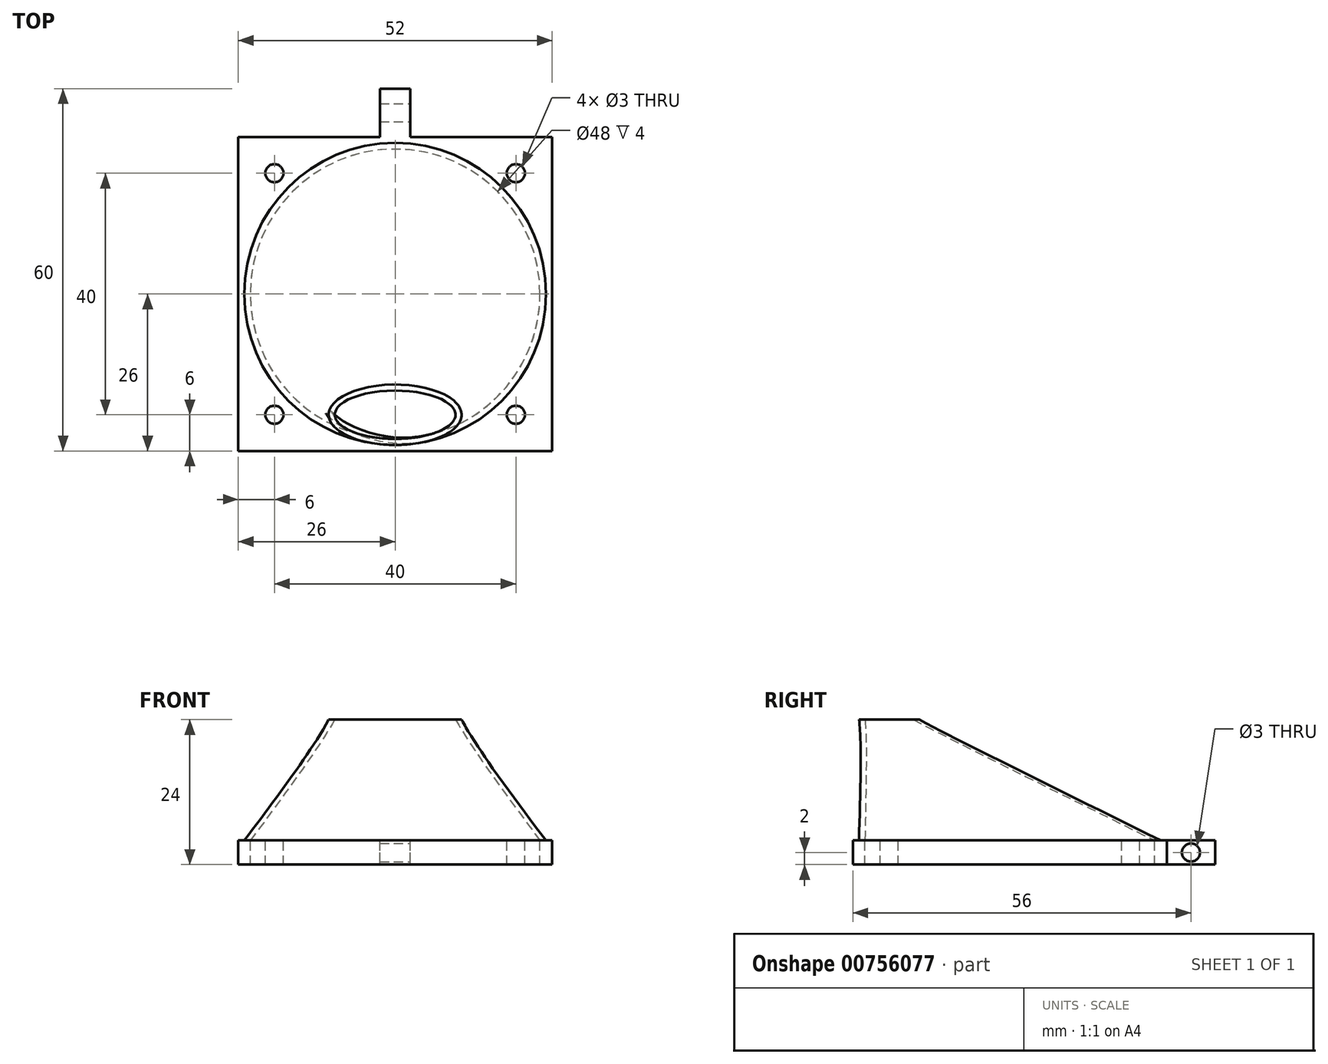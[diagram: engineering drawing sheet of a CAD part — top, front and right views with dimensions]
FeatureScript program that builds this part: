
annotation { "Feature Type Name" : "Feature", "Feature Type Description" : "" }
export const myFeature = defineFeature(function(context is Context, id is Id, definition is map)
    precondition{}
    {
        {
            var Q0;
            Q0=qCreatedBy(makeId("Top.planeOp"),FACE);
            var sketch = newSketch(context, id + "F0", { "sketchPlane" : qUnion([Q0])});
            skPoint(sketch, "E0.middle", {"position": v(0, 0) * mm});
            skCircle(sketch, "E1", {"center": v(0, 0) * mm, "radius": 24 * mm});
            skLineSegment(sketch, "E2.bottom", {"start": v(26, -26) * mm, "end": v(-26, -26) * mm});
            skLineSegment(sketch, "E2.top", {"start": v(26, 26) * mm, "end": v(-26, 26) * mm});
            skLineSegment(sketch, "E2.left", {"start": v(26, -26) * mm, "end": v(26, 26) * mm});
            skLineSegment(sketch, "E2.right", {"start": v(-26, -26) * mm, "end": v(-26, 26) * mm});
            skCircle(sketch, "E3", {"center": v(20, -20) * mm, "radius": 1.5 * mm});
            skCircle(sketch, "E4.MirrorC", {"center": v(-20, -20) * mm, "radius": 1.5 * mm});
            skCircle(sketch, "E5.MirrorC", {"center": v(20, 20) * mm, "radius": 1.5 * mm});
            skCircle(sketch, "E6.MirrorC", {"center": v(-20, 20) * mm, "radius": 1.5 * mm});
            skLineSegment(sketch, "E7.bottom", {"start": v(2.5, 26) * mm, "end": v(-2.5, 26) * mm});
            skLineSegment(sketch, "E7.top", {"start": v(2.5, 34) * mm, "end": v(-2.5, 34) * mm});
            skLineSegment(sketch, "E7.left", {"start": v(2.5, 26) * mm, "end": v(2.5, 34) * mm});
            skLineSegment(sketch, "E7.right", {"start": v(-2.5, 26) * mm, "end": v(-2.5, 34) * mm});
            skPoint(sketch, "E7.middle", {"position": v(0, 30) * mm});
            skLineSegment(sketch, "E8.0", {"start": v(2.5, 30) * mm, "end": v(-2.5, 30) * mm});
            skLineSegment(sketch, "E9.0", {"start": v(2.5, 31.5) * mm, "end": v(-2.5, 31.5) * mm});
            skLineSegment(sketch, "E10.0", {"start": v(2.5, 28.5) * mm, "end": v(-2.5, 28.5) * mm});
            skSolve(sketch);
        }
        {
            var Q0;
            Q0=qCreatedBy(makeId("Top.planeOp"),FACE);
            cPlane(context, id + "F1", {"entities" : qUnion([Q0]), "cplaneType" : CPlaneType.OFFSET, "offset" : 20 * mm, "width" : 150 * mm, "height" : 150 * mm});
        }
        {
            var Q0;
            Q0=qCreatedBy(id+"F1.planeOp",FACE);
            var sketch = newSketch(context, id + "F2", { "sketchPlane" : qUnion([Q0])});
            skEllipse(sketch, "E11", {"center": v(0, -20) * mm, "majorRadius": 10 * mm, "minorRadius": 4 * mm, "majorAxis": v(1, 0)});
            skSolve(sketch);
        }
        {
            var Q0;
            Q0=makeQuery(id+"F0.imprint","IMPRINT",FACE,{"disambiguationData":[TD([[makeQuery(id+"F0.imprint","IMPRINT",EDGE,{"derivedFrom":sQuery(id+"F0.wireOp",EDGE,"E1")}),1.0]])]});
            var Q1;
            Q1=makeQuery(id+"F2.imprint","IMPRINT",FACE,{"disambiguationData":[TD([[makeQuery(id+"F2.imprint","IMPRINT",EDGE,{"derivedFrom":sQuery(id+"F2.wireOp",EDGE,"E11")}),1.0]])]});
            loft(context, id + "F3", {"sheetProfilesArray" : [{ "sheetProfileEntities" : qUnion([Q0]) }, { "sheetProfileEntities" : qUnion([Q1]) }]});
        }
        {
            var Q0;
            Q0=qCreatedBy(makeId("Top.planeOp"),FACE);
            var sketch = newSketch(context, id + "F4", { "sketchPlane" : qUnion([Q0])});
            skCircle(sketch, "E12", {"center": v(0, 0) * mm, "radius": 25 * mm});
            skSolve(sketch);
        }
        {
            var Q0;
            Q0=qCreatedBy(id+"F1.planeOp",FACE);
            var sketch = newSketch(context, id + "F5", { "sketchPlane" : qUnion([Q0])});
            skEllipse(sketch, "E13", {"center": v(0, -20) * mm, "majorRadius": 11 * mm, "minorRadius": 5 * mm, "majorAxis": v(1, 0)});
            skSolve(sketch);
        }
        {
            var Q1;
            Q1=makeQuery(id+"F4.imprint","IMPRINT",FACE,{"disambiguationData":[TD([[makeQuery(id+"F4.imprint","IMPRINT",EDGE,{"derivedFrom":sQuery(id+"F4.wireOp",EDGE,"E12")}),1.0]])]});
            var Q2;
            Q2=makeQuery(id+"F5.imprint","IMPRINT",FACE,{"disambiguationData":[TD([[makeQuery(id+"F5.imprint","IMPRINT",EDGE,{"derivedFrom":sQuery(id+"F5.wireOp",EDGE,"E13")}),1.0]])]});
            loft(context, id + "F6", {"sheetProfilesArray" : [{ "sheetProfileEntities" : qUnion([Q1]) }, { "sheetProfileEntities" : qUnion([Q2]) }]});
        }
        {
            var Q0;
            Q0=makeQuery(id+"F3.opLoft","SWEPT_BODY",BODY,{"disambiguationData":[OSD([makeQuery(id+"F0.imprint","IMPRINT",FACE,{"disambiguationData":[TD([[makeQuery(id+"F0.imprint","IMPRINT",EDGE,{"derivedFrom":sQuery(id+"F0.wireOp",EDGE,"E1")}),1.0]])]}),makeQuery(id+"F2.imprint","IMPRINT",FACE,{"disambiguationData":[TD([[makeQuery(id+"F2.imprint","IMPRINT",EDGE,{"derivedFrom":sQuery(id+"F2.wireOp",EDGE,"E11")}),1.0]])]})])]});
            var Q1;
            Q1=makeQuery(id+"F6.opLoft","SWEPT_BODY",BODY,{"disambiguationData":[OSD([makeQuery(id+"F4.imprint","IMPRINT",FACE,{"disambiguationData":[TD([[makeQuery(id+"F4.imprint","IMPRINT",EDGE,{"derivedFrom":sQuery(id+"F4.wireOp",EDGE,"E12")}),1.0]])]}),makeQuery(id+"F5.imprint","IMPRINT",FACE,{"disambiguationData":[TD([[makeQuery(id+"F5.imprint","IMPRINT",EDGE,{"derivedFrom":sQuery(id+"F5.wireOp",EDGE,"E13")}),1.0]])]})])]});
            booleanBodies(context, id + "F7", {"operationType" : BooleanOperationType.SUBTRACTION, "tools" : qUnion([Q0]), "targets" : qUnion([Q1])});
        }
        {
            var Q0;
            Q0=makeQuery(id+"F0.imprint","IMPRINT",FACE,{"disambiguationData":[TD([[makeQuery(id+"F0.imprint","IMPRINT",EDGE,{"derivedFrom":sQuery(id+"F0.wireOp",EDGE,"E1")}),-1.0]])]});
            var Q1;
            {var subQ5=sQuery(id+"F0.wireOp",EDGE,"E10.0");Q1=makeQuery(id+"F0.imprint","IMPRINT",FACE,{"disambiguationData":[TD([[makeQuery(id+"F0.imprint","IMPRINT",EDGE,{"derivedFrom":subQ5}),1.0]])]});}
            var Q2;
            {var subQ0=sQuery(id+"F0.wireOp",EDGE,"E8.0");Q2=makeQuery(id+"F0.imprint","IMPRINT",FACE,{"disambiguationData":[TD([[makeQuery(id+"F0.imprint","IMPRINT",EDGE,{"derivedFrom":subQ0}),1.0]])]});}
            var Q3;
            {var subQ2=sQuery(id+"F0.wireOp",EDGE,"E8.0");Q3=makeQuery(id+"F0.imprint","IMPRINT",FACE,{"disambiguationData":[TD([[makeQuery(id+"F0.imprint","IMPRINT",EDGE,{"derivedFrom":subQ2}),-1.0]])]});}
            var Q4;
            {var subQ0=sQuery(id+"F0.wireOp",EDGE,"E7.top");Q4=makeQuery(id+"F0.imprint","IMPRINT",FACE,{"disambiguationData":[TD([[makeQuery(id+"F0.imprint","IMPRINT",EDGE,{"derivedFrom":subQ0}),1.0]])]});}
            extrude(context, id + "F8", {"entities" : qUnion([Q0, Q1, Q2, Q3, Q4]), "operationType" : NewBodyOperationType.ADD, "oppositeDirection" : true, "depth" : 4 * mm});
        }
        {
            var Q0;
            {var subQ0=sQuery(id+"F0.wireOp",EDGE,"E8.0");Q0=makeQuery(id+"F0.imprint","IMPRINT",FACE,{"disambiguationData":[TD([[makeQuery(id+"F0.imprint","IMPRINT",EDGE,{"derivedFrom":subQ0}),1.0]])]});}
            var Q1;
            Q1=sQuery(id+"F0.wireOp",EDGE,"E8.0");
            revolve(context, id + "F9", {"entities" : qUnion([Q0]), "axis" : qUnion([Q1]), "revolveType" : RevolveType.FULL});
        }
        {
            var Q0;
            Q0=makeQuery(id+"F9.opRevolve","SWEPT_BODY",BODY,{"disambiguationData":[OSD([sQuery(id+"F0.wireOp",EDGE,"E7.left"),sQuery(id+"F0.wireOp",EDGE,"E7.right"),sQuery(id+"F0.wireOp",EDGE,"E8.0"),sQuery(id+"F0.wireOp",EDGE,"E10.0")])]});
            transform(context, id + "F10", {"entities" : qUnion([Q0]), "transformType" : TransformType.TRANSLATION_3D, "dx" : 0 * mm, "dy" : 0 * mm, "dz" : -2 * mm, "makeCopy" : false});
        }
        {
            var Q0;
            Q0=makeQuery(id+"F9.opRevolve","SWEPT_BODY",BODY,{"disambiguationData":[OSD([sQuery(id+"F0.wireOp",EDGE,"E7.left"),sQuery(id+"F0.wireOp",EDGE,"E7.right"),sQuery(id+"F0.wireOp",EDGE,"E8.0"),sQuery(id+"F0.wireOp",EDGE,"E10.0")])]});
            var Q1;
            Q1=makeQuery(id+"F6.opLoft","SWEPT_BODY",BODY,{"disambiguationData":[OSD([makeQuery(id+"F4.imprint","IMPRINT",FACE,{"disambiguationData":[TD([[makeQuery(id+"F4.imprint","IMPRINT",EDGE,{"derivedFrom":sQuery(id+"F4.wireOp",EDGE,"E12")}),1.0]])]}),makeQuery(id+"F5.imprint","IMPRINT",FACE,{"disambiguationData":[TD([[makeQuery(id+"F5.imprint","IMPRINT",EDGE,{"derivedFrom":sQuery(id+"F5.wireOp",EDGE,"E13")}),1.0]])]})])]});
            booleanBodies(context, id + "F11", {"operationType" : BooleanOperationType.SUBTRACTION, "tools" : qUnion([Q0]), "targets" : qUnion([Q1])});
        }
    });
